# Revit family: Lighting-Terziario-GEWISS-ELIA-CL-LED_PLAFONIERA_TONDA_D300
name_source: partatom
category: Apparecchi per illuminazione
units: mm (PartAtom-declared; Revit-internal decimal feet)

## family parameters
Condiviso = No
Host = Superficie
Punto di calcolo locali = Sì
Quota connettore circolare = Usa diametro
Sorgente d'illuminazione = Sì
Taglio con vuoti quando caricato = No
Tipo di parte = Normale

## types (4) — shared parameters
Angolo inclinazione = -90.00°
Applicazione = Interno
Catalogo = LIGHTING
Catalogo Serie = ELIA CL
Classe isolamento = II
Colore = Bianco
Emetti da lunghezza linea = 610 mm
FORO_CONTROSOFFITTO = 80 mm  [stored 0.262467 ft]
File diagramma fotometrico = GWF1316MA840.IES
Filtro dei colori = 16777215
Grado di protezione = IP20 - IP54
IDF = 95d2ca08-67bb-4880-96e4-8e0345912370
IDT = a0104f8a-d9bd-4c2b-84a2-ea762e196079
Immagine tipo = ELIA_CL.jpg
Installazione = Plafone - Parete
LARGHEZZA_FORO = 820 mm
LED = <Per categoria>
LED Life time (L80B50) = L80 B50 (Tq25°) = 50.000h
LUNGHEZZA FORO = 969 mm
L_lampada = 1500 mm
Lampada: = LED
Lumen output (lm) = 2550
Ottica = Opale diffondente
POSIZIONE = 80000
Potenza di sistema = 25W
Produttore = GEWISS S.p.A.
Prospetto di default = 1219 mm
Resistenza agli urti = IK08
SEO = Plafone - Parete
STRUTTURA = <Per categoria>
Scheda Tecnica = https://www.gewiss.com
Temperatura di colore = 4000K
Temperatura di colore: = 4000K
Tensione = 220-240 VÂ
Tipo lampada = LED
Tipologia = Plafone - Parete
Tipologia sorgente luminosa = LED - Non sostituibile
URL = https://www.gewiss.com
Variazione temperatura colore lampada con luminosità attenuata = <Nessuno>
Versione file RFA = 20.0

## per-type parameters (varying)
| type | Descrizione | Dimensioni (mm) | Garanzia | Modello | Peso (kg) | Peso (kg): | Temperatura di funzionamento | Temperatura di utilizzo |
| GWF1314MA840 - ELIA CL M2 OPAL DIFF 40K ST.ALONE EM | ELIA CL M2 OPAL DIFF 40K ST.ALONE EM | Con Sensore / Emergenza | 3 anni | GWF1314MA840 | 0,8 | 0,8 | -0° +45° | -0° +45° |
| GWF1315MA840 - ELIA CL M2 OPAL DIFF 40K ST.ALONE MW | ELIA CL M2 OPAL DIFF 40K ST.ALONE MW | Con Sensore / Emergenza | 5 anni | GWF1315MA840 | 0,8 | 0,8 | -20° +45° | -20° +45° |
| GWF1310MA840 - ELIA CL M2 OPAL DIFF 40K ST.ALONE ONOFF | ELIA CL M2 OPAL DIFF 40K ST.ALONE ONOFF | Standard | 5 anni | GWF1310MA840 | 0,5 | 0,5 | -20° +45° | -20° +45° |
| GWF1316MA840 - ELIA CL M2 OPAL DIFF 40K ST.ALONE MW EM | ELIA CL M2 OPAL DIFF 40K ST.ALONE MW EM | Con Sensore / Emergenza | 3 anni | GWF1316MA840 | 0,9 | 0,9 | -0° +45° | -0° +45° |

note: [stored X ft] marks values corroborated as IEEE doubles in the binary element streams (Revit-internal decimal feet)
